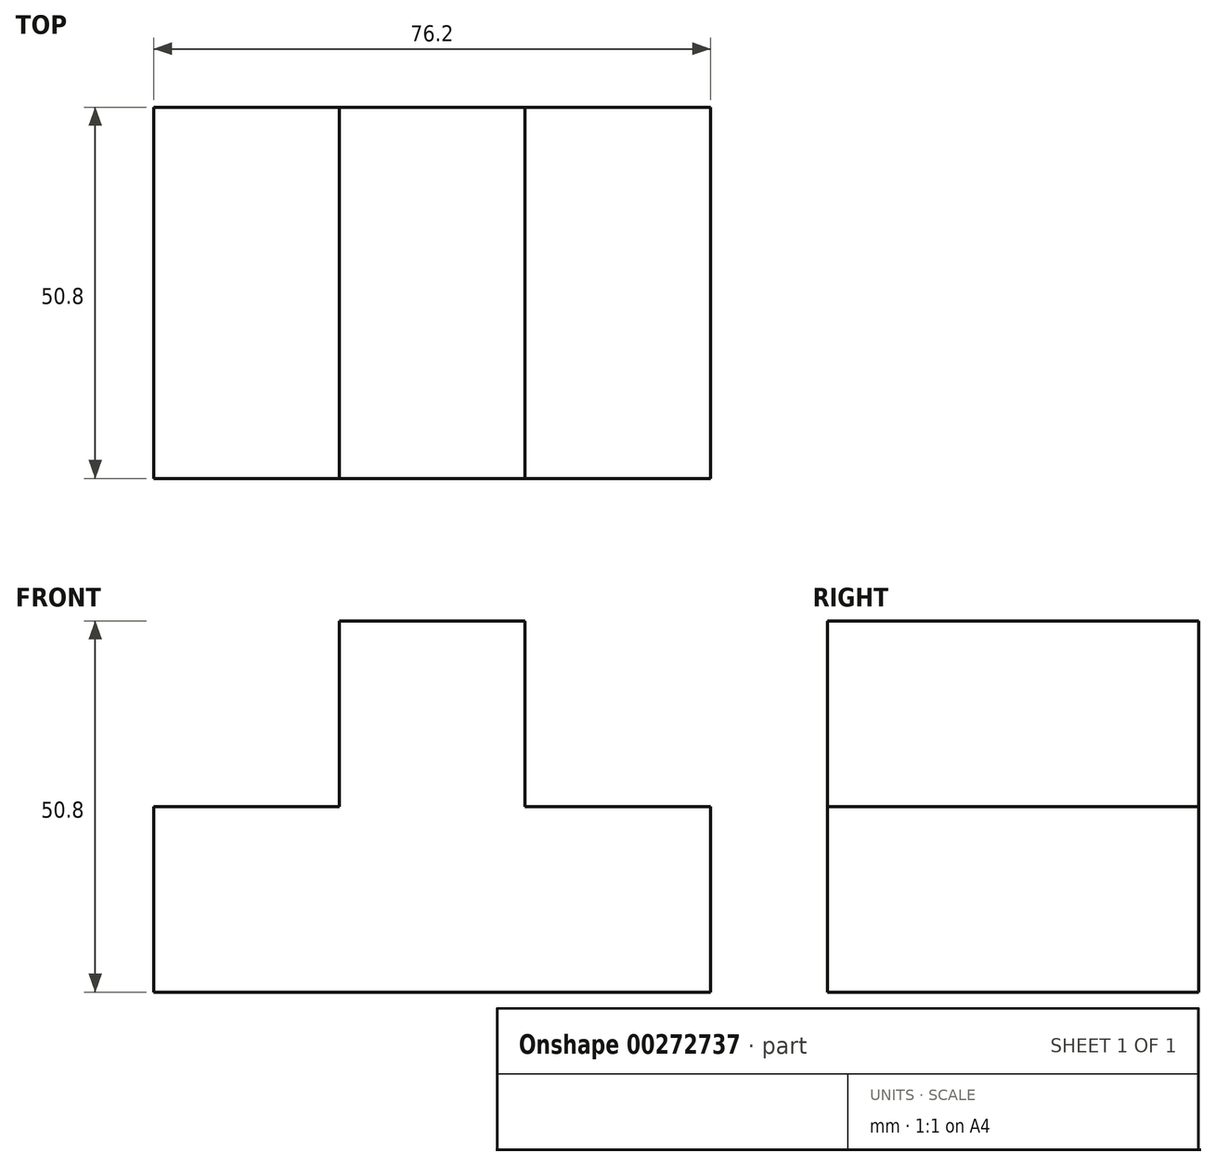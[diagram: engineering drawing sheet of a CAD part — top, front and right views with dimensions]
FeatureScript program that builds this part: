
annotation { "Feature Type Name" : "Feature", "Feature Type Description" : "" }
export const myFeature = defineFeature(function(context is Context, id is Id, definition is map)
    precondition{}
    {
        {
            var Q0;
            Q0=qCreatedBy(makeId("Front.planeOp"),FACE);
            var sketch = newSketch(context, id + "F0", { "sketchPlane" : qUnion([Q0])});
            skLineSegment(sketch, "E0", {"start": v(0, 0) * mm, "end": v(-76.2, 0) * mm});
            skLineSegment(sketch, "E1", {"start": v(-76.2, 0) * mm, "end": v(-76.2, 25.4) * mm});
            skLineSegment(sketch, "E2", {"start": v(-76.2, 25.4) * mm, "end": v(-50.8, 25.4) * mm});
            skLineSegment(sketch, "E3", {"start": v(-50.8, 25.4) * mm, "end": v(-50.8, 50.8) * mm});
            skLineSegment(sketch, "E4", {"start": v(-50.8, 50.8) * mm, "end": v(-25.4, 50.8) * mm});
            skLineSegment(sketch, "E5", {"start": v(-25.4, 50.8) * mm, "end": v(-25.4, 25.4) * mm});
            skLineSegment(sketch, "E6", {"start": v(-25.4, 25.4) * mm, "end": v(0, 25.4) * mm});
            skLineSegment(sketch, "E7", {"start": v(0, 25.4) * mm, "end": v(0, 0) * mm});
            skSolve(sketch);
        }
        {
            var Q0;
            Q0 = qSketchRegion(id + "F0", true);
            extrude(context, id + "F1", {"entities" : qUnion([Q0]), "depth" : 50.8 * mm});
        }
    });
